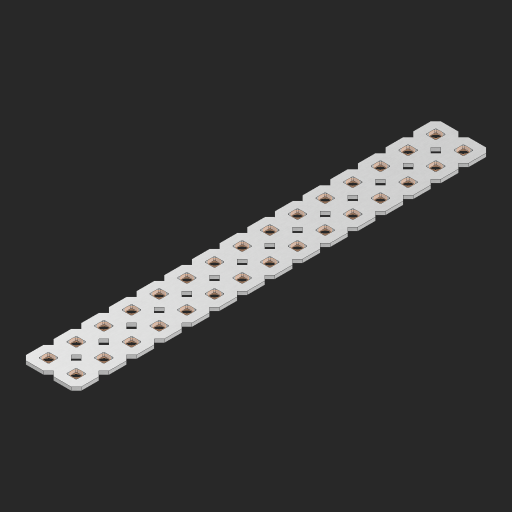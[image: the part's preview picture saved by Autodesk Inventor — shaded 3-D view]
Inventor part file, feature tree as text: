
AUTODESK INVENTOR PART (.ipt)
format: ipt  version: 2023 (Build 270158000, 158)  size: 619,008 bytes
history: native  units: in
note: dims shown in document units (in); Inventor stores cm internally (conversion verified against a paired STEP export)
features: other x31, extrude x29, sketch x2, pattern_linear x1
ambient origin geometry x8: Origin, YZ Plane, XZ Plane, XY Plane, X Axis, Y Axis, Z Axis, Center Point
bodies: Solid1 (feature_tree), Body (feature_tree)
feature tree (63):
  pattern_linear  "Rectangular Pattern1"  Spacing1=0.09in  [1 undecoded]
  sketch  "Sketch1"  dims[d1=0.5in]
  sketch  "Sketch2"  dims[d2=0.182in d3=0.09in d4=0.09in d5=0.09in d6=0.09in d7=0.09in d8=0.09in d9=0.09in d10=0.09in d11=0.02in d13=0.0in d14=0.172in d15=0.0625in d16=0.0in d19=0.5in d22=0.5in]
  other  "Srf1"
  other  "Srf126"
  other  "Srf127"
  other  "Srf128"
  other  "Srf129"
  other  "Srf130"
  other  "Srf131"
  other  "Srf250"
  other  "Srf251"
  other  "Srf252"
  other  "Srf253"
  other  "Srf254"
  other  "Srf255"
  other  "Srf256"
  other  "Srf257"
  other  "Srf268"
  other  "Srf269"
  other  "Srf270"
  other  "Srf271"
  other  "Srf272"
  other  "Srf273"
  other  "Srf274"
  other  "Srf275"
  other  "Srf276"
  other  "Srf277"
  other  "Srf278"
  other  "Srf279"
  other  "Srf280"
  other  "Srf281"
  other  "Srf282"
  other  "Circle"
  extrude  "ExtrusionSrf126"  Depth=0.09in
  extrude  "ExtrusionSrf127"  Depth=0.09in
  extrude  "ExtrusionSrf128"  Depth=0.09in
  extrude  "ExtrusionSrf129"  Depth=0.09in
  extrude  "ExtrusionSrf130"  Depth=0.09in
  extrude  "ExtrusionSrf131"  Depth=0.09in
  extrude  "ExtrusionSrf250"  Depth=0.09in
  extrude  "ExtrusionSrf251"  Depth=0.02in
  extrude  "ExtrusionSrf252"  TaperAngle=0.0deg  [1 undecoded]
  extrude  "ExtrusionSrf253"  Depth=0.5in
  extrude  "ExtrusionSrf254"  Depth=0.0625in TaperAngle=0.0deg
  extrude  "ExtrusionSrf255"  Depth=0.5in
  extrude  "ExtrusionSrf256"  Depth=0.5in
  extrude  "ExtrusionSrf257"  [1 undecoded]
  extrude  "ExtrusionSrf268"  [1 undecoded]
  extrude  "ExtrusionSrf269"  [1 undecoded]
  extrude  "ExtrusionSrf270"  [1 undecoded]
  extrude  "ExtrusionSrf271"  [1 undecoded]
  extrude  "ExtrusionSrf272"  [1 undecoded]
  extrude  "ExtrusionSrf273"  [1 undecoded]
  extrude  "ExtrusionSrf274"  [1 undecoded]
  extrude  "ExtrusionSrf275"  [1 undecoded]
  extrude  "ExtrusionSrf276"  [1 undecoded]
  extrude  "ExtrusionSrf277"  [1 undecoded]
  extrude  "ExtrusionSrf278"  [1 undecoded]
  extrude  "ExtrusionSrf279"  [1 undecoded]
  extrude  "ExtrusionSrf280"  [1 undecoded]
  extrude  "ExtrusionSrf281"  [1 undecoded]
  extrude  "ExtrusionSrf282"  [1 undecoded]
note: 18 required parameter values undecoded (feature->parameter linkage not recoverable at this tier; creation-order binding heuristic only, values carry confidence <= 0.55)
